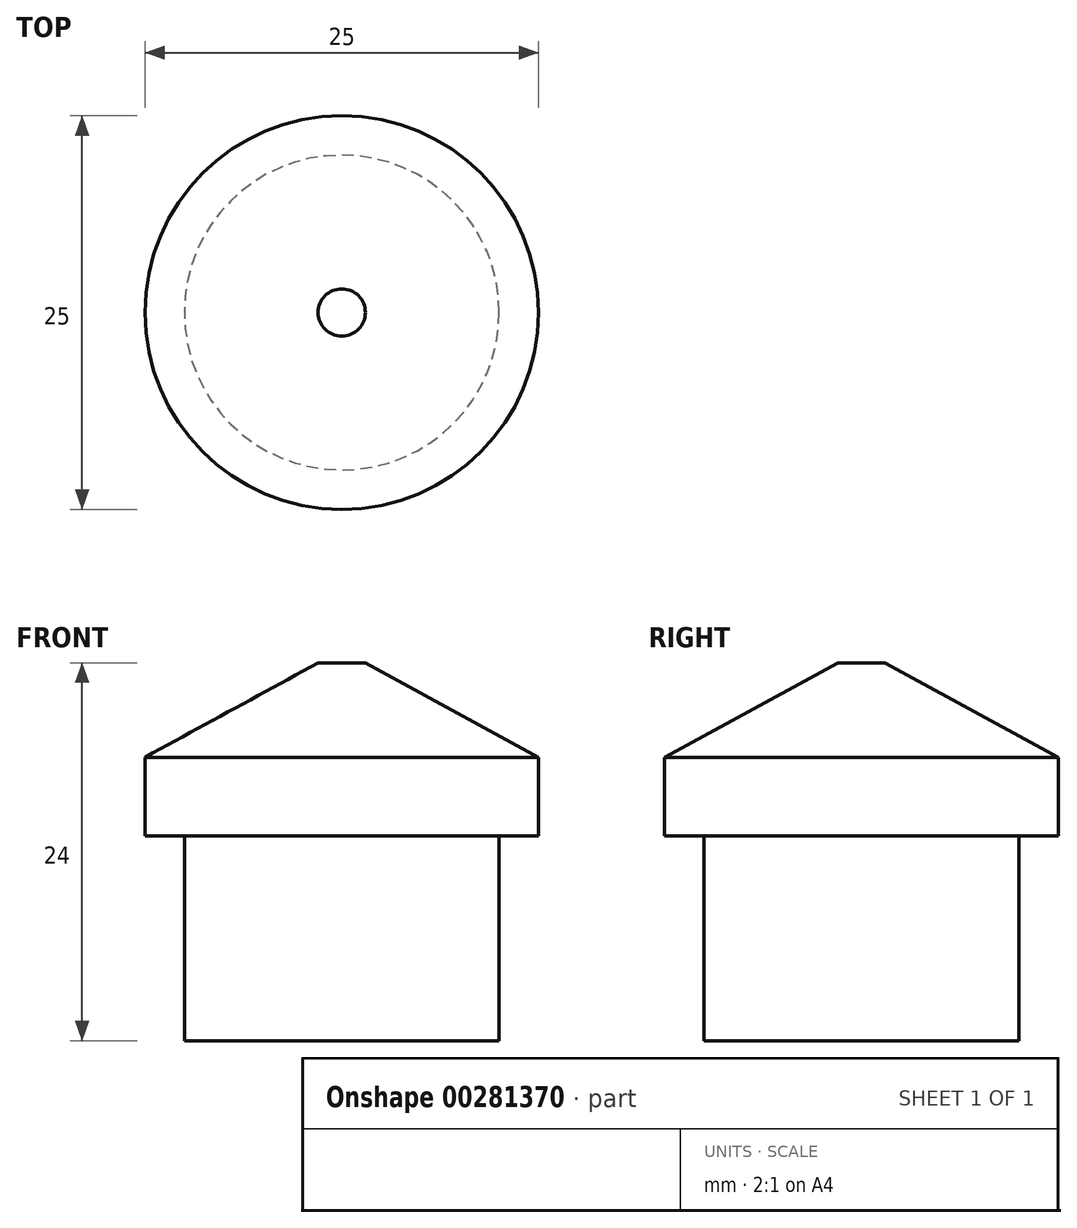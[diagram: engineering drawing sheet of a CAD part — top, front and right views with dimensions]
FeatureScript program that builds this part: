
annotation { "Feature Type Name" : "Feature", "Feature Type Description" : "" }
export const myFeature = defineFeature(function(context is Context, id is Id, definition is map)
    precondition{}
    {
        {
            var Q0;
            Q0=qCreatedBy(makeId("Front.planeOp"),FACE);
            var sketch = newSketch(context, id + "F0", { "sketchPlane" : qUnion([Q0])});
            skLineSegment(sketch, "E0", {"start": v(0, 0) * mm, "end": v(0, 24) * mm});
            skLineSegment(sketch, "E1", {"start": v(0, 24) * mm, "end": v(1.5, 24) * mm});
            skLineSegment(sketch, "E2", {"start": v(1.5, 24) * mm, "end": v(12.5, 18) * mm});
            skLineSegment(sketch, "E3", {"start": v(12.5, 18) * mm, "end": v(12.5, 13) * mm});
            skLineSegment(sketch, "E4", {"start": v(12.5, 13) * mm, "end": v(10, 13) * mm});
            skLineSegment(sketch, "E5", {"start": v(10, 13) * mm, "end": v(10, 0) * mm});
            skLineSegment(sketch, "E6", {"start": v(10, 0) * mm, "end": v(0, 0) * mm});
            skSolve(sketch);
        }
        {
            var Q0;
            Q0=makeQuery(id+"F0.imprint","IMPRINT",FACE,{"disambiguationData":[TD([[makeQuery(id+"F0.imprint","IMPRINT",EDGE,{"derivedFrom":sQuery(id+"F0.wireOp",EDGE,"E0")}),-1.0]])]});
            var Q1;
            Q1=sQuery(id+"F0.wireOp",EDGE,"E0");
            revolve(context, id + "F1", {"entities" : qUnion([Q0]), "axis" : qUnion([Q1]), "revolveType" : RevolveType.FULL});
        }
    });
